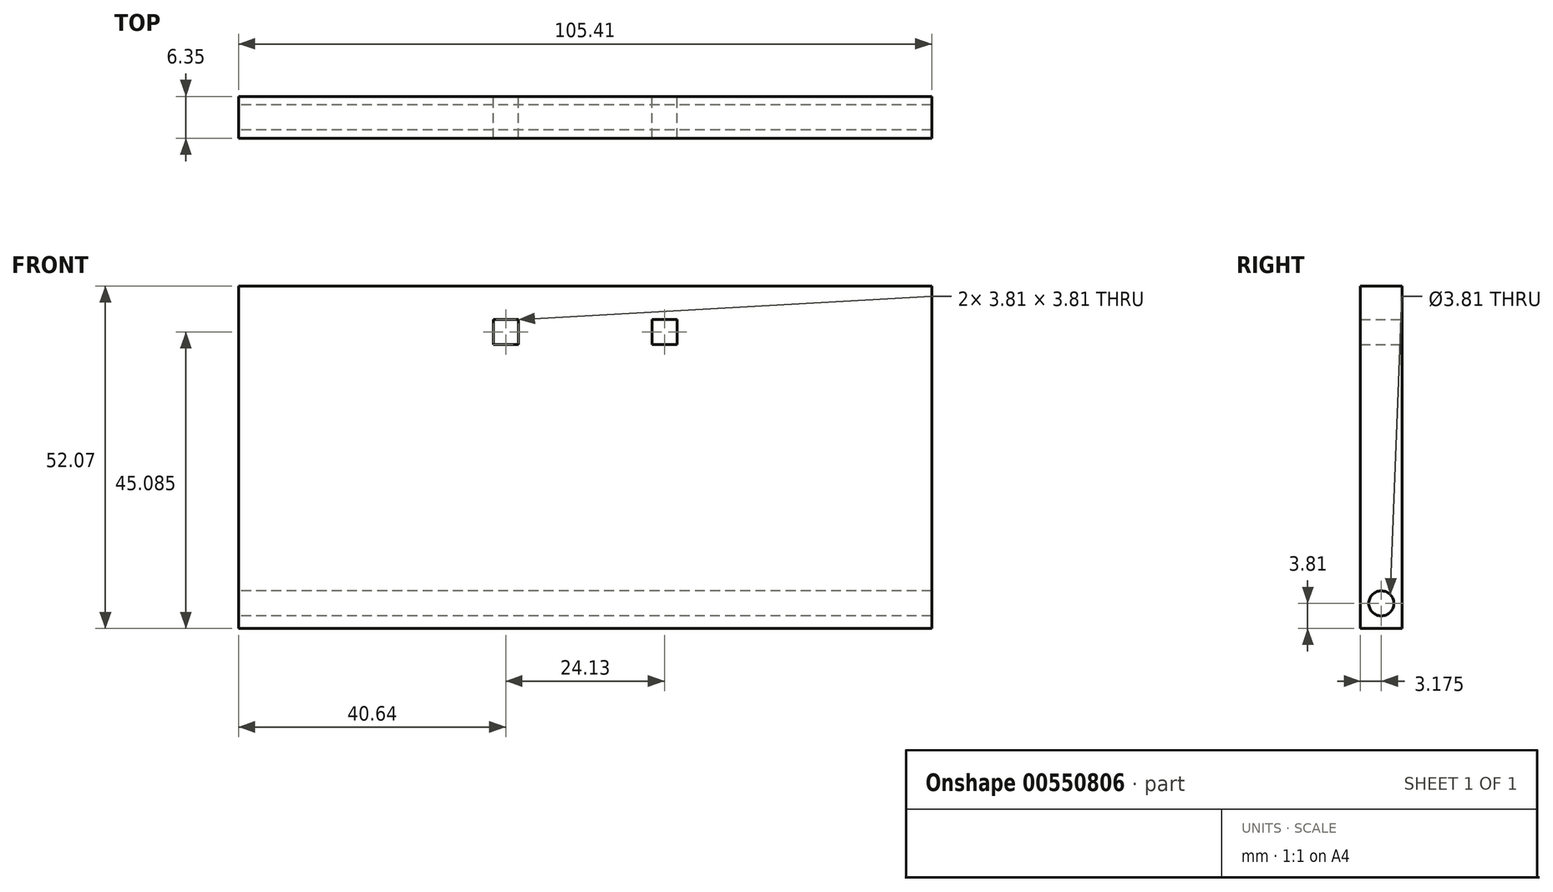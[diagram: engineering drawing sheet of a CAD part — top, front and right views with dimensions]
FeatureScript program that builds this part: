
annotation { "Feature Type Name" : "Feature", "Feature Type Description" : "" }
export const myFeature = defineFeature(function(context is Context, id is Id, definition is map)
    precondition{}
    {
        {
            var Q0;
            Q0=qCreatedBy(makeId("Front.planeOp"),FACE);
            var sketch = newSketch(context, id + "F0", { "sketchPlane" : qUnion([Q0])});
            skLineSegment(sketch, "E0.bottom", {"start": v(0, 0) * mm, "end": v(105.41, 0) * mm});
            skLineSegment(sketch, "E0.top", {"start": v(0, -52.07) * mm, "end": v(105.41, -52.07) * mm});
            skLineSegment(sketch, "E0.left", {"start": v(0, 0) * mm, "end": v(0, -52.07) * mm});
            skLineSegment(sketch, "E0.right", {"start": v(105.41, 0) * mm, "end": v(105.41, -52.07) * mm});
            skLineSegment(sketch, "E1", {"start": v(52.7, 0) * mm, "end": v(52.7, -52.07) * mm, "construction": true});
            skLineSegment(sketch, "E2.bottom", {"start": v(38.74, -5.08) * mm, "end": v(42.55, -5.08) * mm});
            skLineSegment(sketch, "E2.top", {"start": v(38.74, -8.9) * mm, "end": v(42.55, -8.9) * mm});
            skLineSegment(sketch, "E2.left", {"start": v(38.74, -5.08) * mm, "end": v(38.74, -8.9) * mm});
            skLineSegment(sketch, "E2.right", {"start": v(42.55, -5.08) * mm, "end": v(42.55, -8.9) * mm});
            skLineSegment(sketch, "E3.bottom", {"start": v(62.87, -5.08) * mm, "end": v(66.67, -5.08) * mm});
            skLineSegment(sketch, "E3.top", {"start": v(62.87, -8.9) * mm, "end": v(66.67, -8.9) * mm});
            skLineSegment(sketch, "E3.left", {"start": v(62.87, -5.08) * mm, "end": v(62.87, -8.9) * mm});
            skLineSegment(sketch, "E3.right", {"start": v(66.67, -5.08) * mm, "end": v(66.67, -8.9) * mm});
            skSolve(sketch);
        }
        {
            var Q0;
            Q0=makeQuery(id+"F0.imprint","IMPRINT",FACE,{"disambiguationData":[TD([[makeQuery(id+"F0.imprint","IMPRINT",EDGE,{"derivedFrom":sQuery(id+"F0.wireOp",EDGE,"E0.bottom")}),-1.0]])]});
            extrude(context, id + "F1", {"entities" : qUnion([Q0]), "depth" : 6.35 * mm, "offsetDistance" : 25.4 * mm});
        }
        {
            var Q0;
            Q0=qCreatedBy(makeId("Right.planeOp"),FACE);
            var sketch = newSketch(context, id + "F2", { "sketchPlane" : qUnion([Q0])});
            skCircle(sketch, "E4", {"center": v(-3.18, -48.26) * mm, "radius": 1.9 * mm});
            skSolve(sketch);
        }
        {
            var Q0;
            Q0=makeQuery(id+"F2.imprint","IMPRINT",FACE,{"disambiguationData":[TD([[makeQuery(id+"F2.imprint","IMPRINT",EDGE,{"derivedFrom":sQuery(id+"F2.wireOp",EDGE,"E4")}),1.0]])]});
            extrude(context, id + "F3", {"entities" : qUnion([Q0]), "operationType" : NewBodyOperationType.REMOVE, "endBound" : BoundingType.THROUGH_ALL, "depth" : 25.4 * mm, "offsetDistance" : 25.4 * mm});
        }
    });
